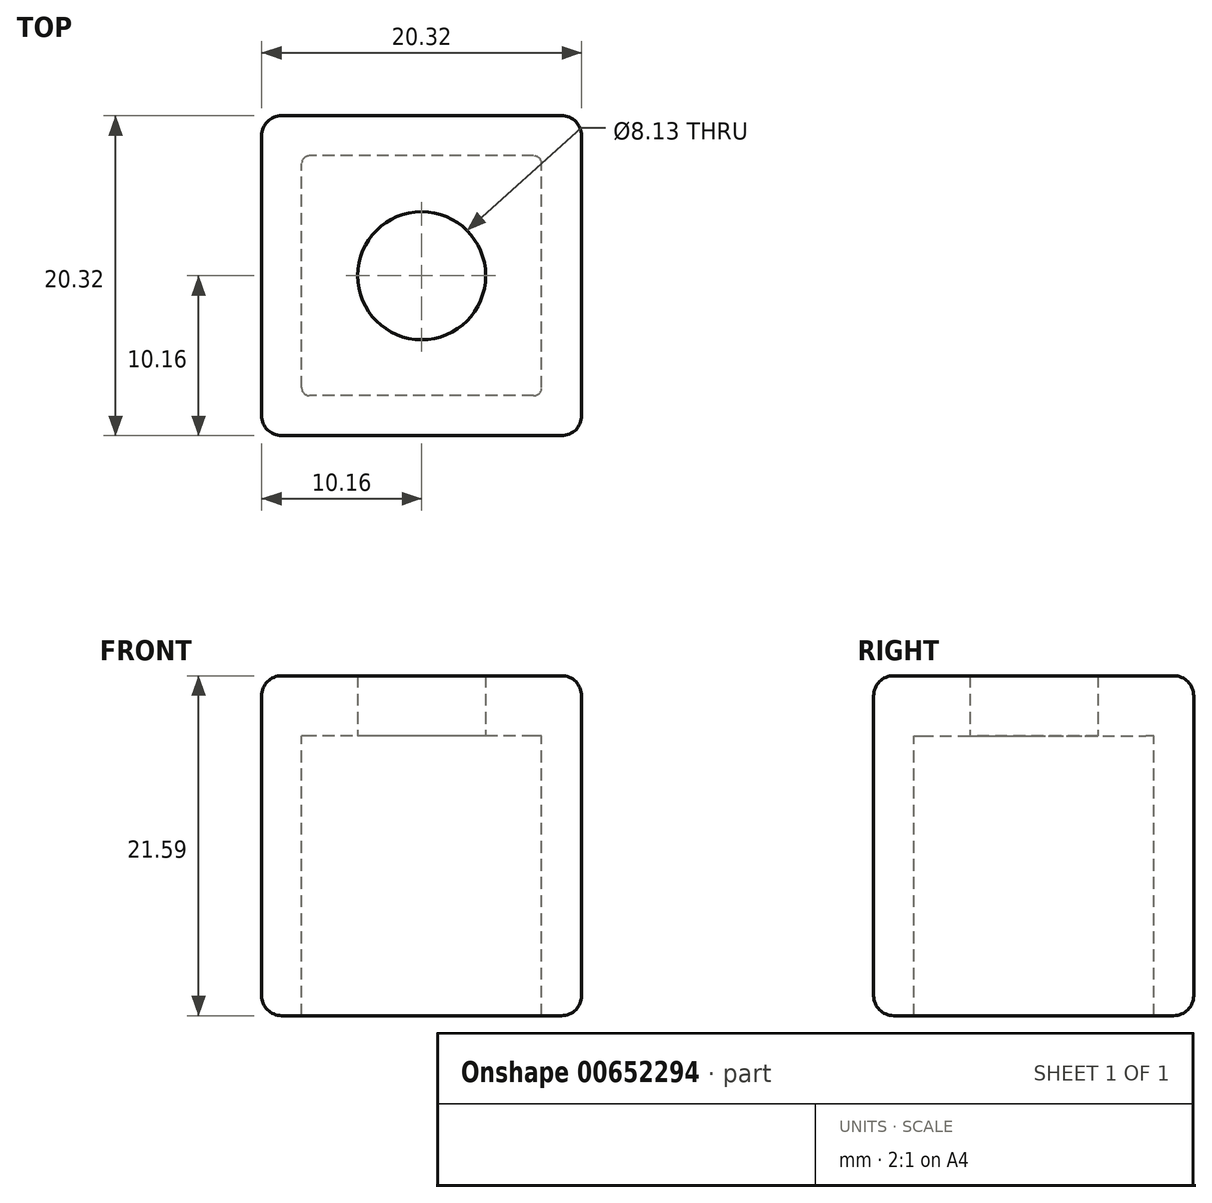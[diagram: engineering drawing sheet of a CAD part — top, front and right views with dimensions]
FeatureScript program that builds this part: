
annotation { "Feature Type Name" : "Feature", "Feature Type Description" : "" }
export const myFeature = defineFeature(function(context is Context, id is Id, definition is map)
    precondition{}
    {
        {
            var Q0;
            Q0=qCreatedBy(makeId("Top.planeOp"),FACE);
            var sketch = newSketch(context, id + "F0", { "sketchPlane" : qUnion([Q0])});
            skLineSegment(sketch, "E0.bottom", {"start": v(10.16, -10.16) * mm, "end": v(-10.16, -10.16) * mm});
            skLineSegment(sketch, "E0.top", {"start": v(10.16, 10.16) * mm, "end": v(-10.16, 10.16) * mm});
            skLineSegment(sketch, "E0.left", {"start": v(10.16, -10.16) * mm, "end": v(10.16, 10.16) * mm});
            skLineSegment(sketch, "E0.right", {"start": v(-10.16, -10.16) * mm, "end": v(-10.16, 10.16) * mm});
            skPoint(sketch, "E0.middle", {"position": v(0, 0) * mm});
            skLineSegment(sketch, "E1.0", {"start": v(7.62, -7.62) * mm, "end": v(7.62, 7.62) * mm});
            skLineSegment(sketch, "E1.1", {"start": v(7.62, -7.62) * mm, "end": v(-7.62, -7.62) * mm});
            skLineSegment(sketch, "E1.2", {"start": v(-7.62, -7.62) * mm, "end": v(-7.62, 7.62) * mm});
            skLineSegment(sketch, "E1.3", {"start": v(7.62, 7.62) * mm, "end": v(-7.62, 7.62) * mm});
            skSolve(sketch);
        }
        {
            var Q0;
            Q0=makeQuery(id+"F0.imprint","IMPRINT",FACE,{"disambiguationData":[TD([[makeQuery(id+"F0.imprint","IMPRINT",EDGE,{"derivedFrom":sQuery(id+"F0.wireOp",EDGE,"E1.0")}),1.0]])]});
            var Q1;
            Q1=makeQuery(id+"F0.imprint","IMPRINT",FACE,{"disambiguationData":[TD([[makeQuery(id+"F0.imprint","IMPRINT",EDGE,{"derivedFrom":sQuery(id+"F0.wireOp",EDGE,"E0.bottom")}),-1.0]])]});
            extrude(context, id + "F1", {"entities" : qUnion([Q0, Q1]), "depth" : 3.8 * mm, "offsetDistance" : 25.4 * mm});
        }
        {
            var Q0;
            Q0=makeQuery(id+"F0.imprint","IMPRINT",FACE,{"disambiguationData":[TD([[makeQuery(id+"F0.imprint","IMPRINT",EDGE,{"derivedFrom":sQuery(id+"F0.wireOp",EDGE,"E0.bottom")}),-1.0]])]});
            extrude(context, id + "F2", {"entities" : qUnion([Q0]), "operationType" : NewBodyOperationType.ADD, "oppositeDirection" : true, "depth" : 17.78 * mm, "offsetDistance" : 25.4 * mm});
        }
        {
            var Q0;
            Q0=qCreatedBy(makeId("Top.planeOp"),FACE);
            var sketch = newSketch(context, id + "F3", { "sketchPlane" : qUnion([Q0])});
            skCircle(sketch, "E2", {"center": v(0, 0) * mm, "radius": 4.06 * mm});
            skSolve(sketch);
        }
        {
            var Q0;
            Q0=makeQuery(id+"F3.imprint","IMPRINT",FACE,{"disambiguationData":[TD([[makeQuery(id+"F3.imprint","IMPRINT",EDGE,{"derivedFrom":sQuery(id+"F3.wireOp",EDGE,"E2")}),1.0]])]});
            extrude(context, id + "F4", {"entities" : qUnion([Q0]), "operationType" : NewBodyOperationType.REMOVE, "depth" : 25.4 * mm, "offsetDistance" : 25.4 * mm});
        }
        {
            var Q0;
            Q0=makeQuery(id+"F1.opExtrude","CAP_EDGE",EDGE,{"disambiguationData":[OSD([sQuery(id+"F0.wireOp",EDGE,"E0.right")])],"isStart":false});
            var Q1;
            Q1=makeQuery(id+"F1.opExtrude","CAP_EDGE",EDGE,{"disambiguationData":[OSD([sQuery(id+"F0.wireOp",EDGE,"E0.top")])],"isStart":false});
            var Q2;
            Q2=makeQuery(id+"F1.opExtrude","CAP_EDGE",EDGE,{"disambiguationData":[OSD([sQuery(id+"F0.wireOp",EDGE,"E0.left")])],"isStart":false});
            var Q3;
            Q3=makeQuery(id+"F1.opExtrude","CAP_EDGE",EDGE,{"disambiguationData":[OSD([sQuery(id+"F0.wireOp",EDGE,"E0.bottom")])],"isStart":false});
            var Q4;
            {var subQ0=sQuery(id+"F0.wireOp",EDGE,"E0.right");Q4=makeQuery(id+"F2.boolean.opBoolean","MERGE",FACE,{"derivedFrom":[makeQuery(id+"F1.opExtrude","SWEPT_FACE",FACE,{"disambiguationData":[OSD([subQ0])]}),makeQuery(id+"F2.opExtrude","SWEPT_FACE",FACE,{"disambiguationData":[OSD([subQ0])]})]});}
            var Q5;
            {var subQ0=sQuery(id+"F0.wireOp",EDGE,"E0.left");Q5=makeQuery(id+"F2.boolean.opBoolean","MERGE",FACE,{"derivedFrom":[makeQuery(id+"F1.opExtrude","SWEPT_FACE",FACE,{"disambiguationData":[OSD([subQ0])]}),makeQuery(id+"F2.opExtrude","SWEPT_FACE",FACE,{"disambiguationData":[OSD([subQ0])]})]});}
            var Q6;
            Q6=makeQuery(id+"F2.opExtrude","CAP_EDGE",EDGE,{"disambiguationData":[OSD([sQuery(id+"F0.wireOp",EDGE,"E0.bottom")])],"isStart":false});
            var Q7;
            Q7=makeQuery(id+"F2.opExtrude","CAP_EDGE",EDGE,{"disambiguationData":[OSD([sQuery(id+"F0.wireOp",EDGE,"E0.top")])],"isStart":false});
            fillet(context, id + "F5", {"entities" : qUnion([Q0, Q1, Q2, Q3, Q4, Q5, Q6, Q7]), "radius" : 1.27 * mm, "tangentPropagation" : true, "allowEdgeOverflow" : false});
        }
        {
            var Q0;
            Q0=makeQuery(id+"F2.opExtrude","SWEPT_EDGE",EDGE,{"disambiguationData":[OSD([sQuery(id+"F0.wireOp",EDGE,"E1.1"),sQuery(id+"F0.wireOp",EDGE,"E1.2")])]});
            var Q1;
            Q1=makeQuery(id+"F2.opExtrude","SWEPT_EDGE",EDGE,{"disambiguationData":[OSD([sQuery(id+"F0.wireOp",EDGE,"E1.0"),sQuery(id+"F0.wireOp",EDGE,"E1.1")])]});
            var Q2;
            Q2=makeQuery(id+"F2.opExtrude","SWEPT_EDGE",EDGE,{"disambiguationData":[OSD([sQuery(id+"F0.wireOp",EDGE,"E1.0"),sQuery(id+"F0.wireOp",EDGE,"E1.3")])]});
            var Q3;
            Q3=makeQuery(id+"F2.opExtrude","SWEPT_EDGE",EDGE,{"disambiguationData":[OSD([sQuery(id+"F0.wireOp",EDGE,"E1.2"),sQuery(id+"F0.wireOp",EDGE,"E1.3")])]});
            fillet(context, id + "F6", {"entities" : qUnion([Q0, Q1, Q2, Q3]), "radius" : 0.5 * mm, "tangentPropagation" : true, "allowEdgeOverflow" : false});
        }
    });
